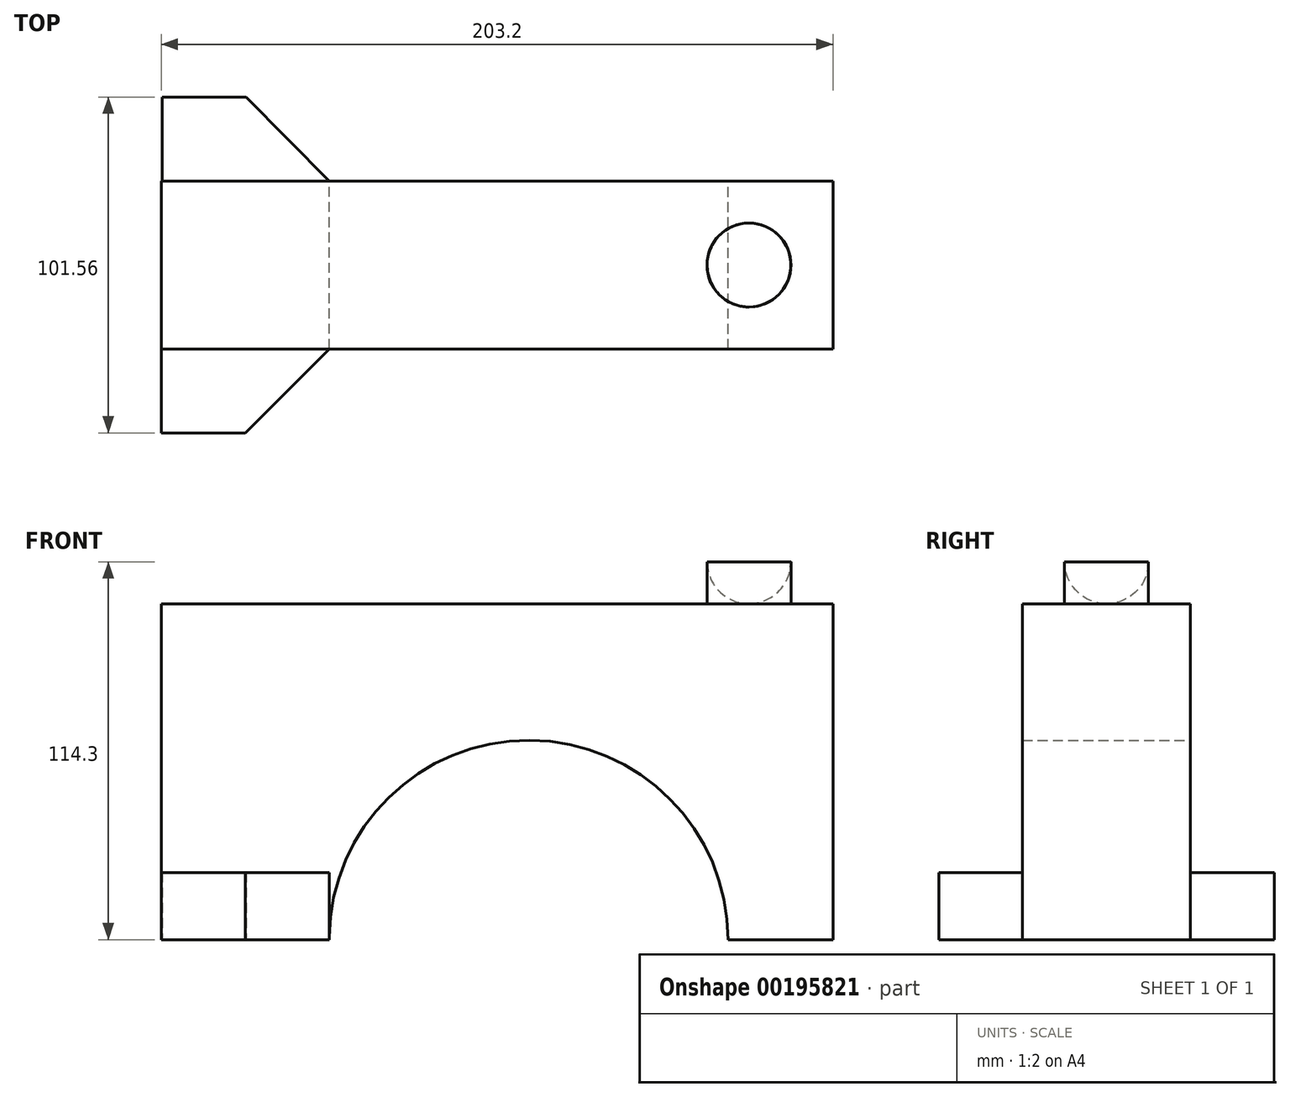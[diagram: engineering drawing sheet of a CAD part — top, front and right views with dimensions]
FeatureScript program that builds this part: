
annotation { "Feature Type Name" : "Feature", "Feature Type Description" : "" }
export const myFeature = defineFeature(function(context is Context, id is Id, definition is map)
    precondition{}
    {
        {
            var Q0;
            Q0=qCreatedBy(makeId("Front.planeOp"),FACE);
            var sketch = newSketch(context, id + "F0", { "sketchPlane" : qUnion([Q0])});
            skLineSegment(sketch, "E0.bottom", {"start": v(-101.6, 50.8) * mm, "end": v(101.6, 50.8) * mm});
            skLineSegment(sketch, "E0.top", {"start": v(-101.6, -50.8) * mm, "end": v(101.6, -50.8) * mm});
            skLineSegment(sketch, "E0.left", {"start": v(-101.6, 50.8) * mm, "end": v(-101.6, -50.8) * mm});
            skLineSegment(sketch, "E0.right", {"start": v(101.6, 50.8) * mm, "end": v(101.6, -50.8) * mm});
            skPoint(sketch, "E0.middle", {"position": v(0, 0) * mm});
            skArc(sketch, "E1", {"start": v(69.85, -50.8) * mm, "mid": v(9.52, 9.52) * mm, "end": v(-50.8, -50.8) * mm});
            skSolve(sketch);
        }
        {
            var Q0;
            Q0=makeQuery(id+"F0.imprint","IMPRINT",FACE,{"disambiguationData":[TD([[makeQuery(id+"F0.imprint","IMPRINT",EDGE,{"derivedFrom":sQuery(id+"F0.wireOp",EDGE,"E0.bottom")}),-1.0]])]});
            extrude(context, id + "F1", {"entities" : qUnion([Q0]), "depth" : 25.4 * mm, "hasSecondDirection" : true, "secondDirectionOppositeDirection" : true, "secondDirectionDepth" : 25.4 * mm});
        }
        {
            var Q0;
            Q0=qCreatedBy(makeId("Top.planeOp"),FACE);
            cPlane(context, id + "F2", {"entities" : qUnion([Q0]), "cplaneType" : CPlaneType.OFFSET, "offset" : 50.8 * mm, "width" : 152.4 * mm, "height" : 152.4 * mm});
        }
        {
            var Q0;
            Q0=qCreatedBy(id+"F2.planeOp",FACE);
            var sketch = newSketch(context, id + "F3", { "sketchPlane" : qUnion([Q0])});
            skCircle(sketch, "E2", {"center": v(76.2, 0) * mm, "radius": 12.7 * mm});
            skSolve(sketch);
        }
        {
            var Q0;
            Q0=makeQuery(id+"F3.imprint","IMPRINT",FACE,{"disambiguationData":[TD([[makeQuery(id+"F3.imprint","IMPRINT",EDGE,{"derivedFrom":sQuery(id+"F3.wireOp",EDGE,"E2")}),1.0]])]});
            extrude(context, id + "F4", {"entities" : qUnion([Q0]), "operationType" : NewBodyOperationType.ADD, "depth" : 12.7 * mm});
        }
        {
            var Q0;
            Q0=qCreatedBy(makeId("Front.planeOp"),FACE);
            var sketch = newSketch(context, id + "F5", { "sketchPlane" : qUnion([Q0])});
            skLineSegment(sketch, "E3", {"start": v(88.85, 63.47) * mm, "end": v(63.56, 63.53) * mm});
            skArc(sketch, "E4", {"start": v(88.85, 63.47) * mm, "mid": v(76.23, 76.2) * mm, "end": v(63.56, 63.53) * mm});
            skSolve(sketch);
        }
        {
            var Q0;
            Q0=makeQuery(id+"F5.imprint","IMPRINT",FACE,{"disambiguationData":[TD([[makeQuery(id+"F5.imprint","IMPRINT",EDGE,{"derivedFrom":sQuery(id+"F5.wireOp",EDGE,"E3")}),-1.0]])]});
            var Q1;
            Q1=sQuery(id+"F5.wireOp",EDGE,"E3");
            revolve(context, id + "F6", {"operationType" : NewBodyOperationType.ADD, "entities" : qUnion([Q0]), "axis" : qUnion([Q1]), "revolveType" : RevolveType.FULL});
        }
        {
            var Q0;
            Q0=qCreatedBy(makeId("Top.planeOp"),FACE);
            cPlane(context, id + "F7", {"entities" : qUnion([Q0]), "cplaneType" : CPlaneType.OFFSET, "offset" : 50.8 * mm, "oppositeDirection" : true, "width" : 152.4 * mm, "height" : 152.4 * mm});
        }
        {
            var Q0;
            Q0=qCreatedBy(id+"F7.planeOp",FACE);
            var sketch = newSketch(context, id + "F8", { "sketchPlane" : qUnion([Q0])});
            skLineSegment(sketch, "E5.bottom", {"start": v(-101.35, 50.8) * mm, "end": v(-75.95, 50.8) * mm});
            skLineSegment(sketch, "E5.top", {"start": v(-101.35, 25.4) * mm, "end": v(-75.95, 25.4) * mm});
            skLineSegment(sketch, "E5.left", {"start": v(-101.35, 50.8) * mm, "end": v(-101.35, 25.4) * mm});
            skLineSegment(sketch, "E5.right", {"start": v(-75.95, 50.8) * mm, "end": v(-75.95, 25.4) * mm});
            skPoint(sketch, "E5.middle", {"position": v(-88.65, 38.1) * mm});
            skLineSegment(sketch, "E6.bottom", {"start": v(-101.54, -50.76) * mm, "end": v(-76.14, -50.76) * mm});
            skLineSegment(sketch, "E6.top", {"start": v(-101.54, -25.36) * mm, "end": v(-76.14, -25.36) * mm});
            skLineSegment(sketch, "E6.left", {"start": v(-101.54, -50.76) * mm, "end": v(-101.54, -25.36) * mm});
            skLineSegment(sketch, "E6.right", {"start": v(-76.14, -50.76) * mm, "end": v(-76.14, -25.36) * mm});
            skPoint(sketch, "E6.middle", {"position": v(-88.84, -38.06) * mm});
            skLineSegment(sketch, "E7", {"start": v(-75.95, 25.4) * mm, "end": v(-50.74, 25.4) * mm});
            skLineSegment(sketch, "E8", {"start": v(-50.74, 25.4) * mm, "end": v(-75.95, 50.8) * mm});
            skLineSegment(sketch, "E9", {"start": v(-76.14, -50.76) * mm, "end": v(-50.74, -25.34) * mm});
            skLineSegment(sketch, "E10", {"start": v(-50.74, -25.34) * mm, "end": v(-76.14, -25.36) * mm});
            skSolve(sketch);
        }
        {
            var Q0;
            Q0=makeQuery(id+"F8.imprint","IMPRINT",FACE,{"disambiguationData":[TD([[makeQuery(id+"F8.imprint","IMPRINT",EDGE,{"derivedFrom":sQuery(id+"F8.wireOp",EDGE,"E5.bottom")}),-1.0]])]});
            var Q1;
            Q1=makeQuery(id+"F8.imprint","IMPRINT",FACE,{"disambiguationData":[TD([[makeQuery(id+"F8.imprint","IMPRINT",EDGE,{"derivedFrom":sQuery(id+"F8.wireOp",EDGE,"E5.right")}),1.0]])]});
            var Q2;
            Q2=makeQuery(id+"F8.imprint","IMPRINT",FACE,{"disambiguationData":[TD([[makeQuery(id+"F8.imprint","IMPRINT",EDGE,{"derivedFrom":sQuery(id+"F8.wireOp",EDGE,"E6.right")}),-1.0]])]});
            var Q3;
            Q3=makeQuery(id+"F8.imprint","IMPRINT",FACE,{"disambiguationData":[TD([[makeQuery(id+"F8.imprint","IMPRINT",EDGE,{"derivedFrom":sQuery(id+"F8.wireOp",EDGE,"E6.bottom")}),1.0]])]});
            extrude(context, id + "F9", {"entities" : qUnion([Q0, Q1, Q2, Q3]), "operationType" : NewBodyOperationType.ADD, "depth" : 20.32 * mm});
        }
    });
